# Revit family: Furniture-Wall_Mount-Cabinet-KOHLER-Grooming-K-33694.rfa_
name_source: partatom
category: Casework
units: mm (PartAtom-declared; Revit-internal decimal feet)

## family parameters
Cut with Voids When Loaded = No
Host = Face
OmniClass Number = 23.21.19.00
OmniClass Title = Casework
Room Calculation Point = No
Shared = No

## types (2) — shared parameters
ADA Compliant = No
Assembly Code = E2010.30
Date Modified = 05/16/2023
Default Elevation = 60"
Depth = 4 15/16"
Finish = Kohler-Metal-NA-Black
Hardware Included = No
Height = 31 11/16"
Manufacturer = Kohler Co.
Master Format 2014 = 12 35 30.23
Master Format 2014 Name = Bathroom Casework
Material = Aluminium
Product Documentation Link = https://www.us.kohler.com
Product Finish = Kohler-Metal-NA-Black
Product Name = Grooming
Product Page URL = http://www.us.kohler.com
URL = https://www.us.kohler.com
WaterSense Certified = No
Width = 11 13/16"

## per-type parameters (varying)
| type | Description | Left Side | Model | Right Side | Type |
| Left Side, NA-Black | 300 MM Basic Side Cabinet Left Open | Yes | K-33694-L-NA | No | 1 |
| Right Side, NA-Black | 300 MM Basic Side Cabinet Right Open | No | K-33694-R-NA | Yes | 2 |

## geometry (parser evidence)
native form markers: Sweep x6
no freeform markers — native parametric forms only
